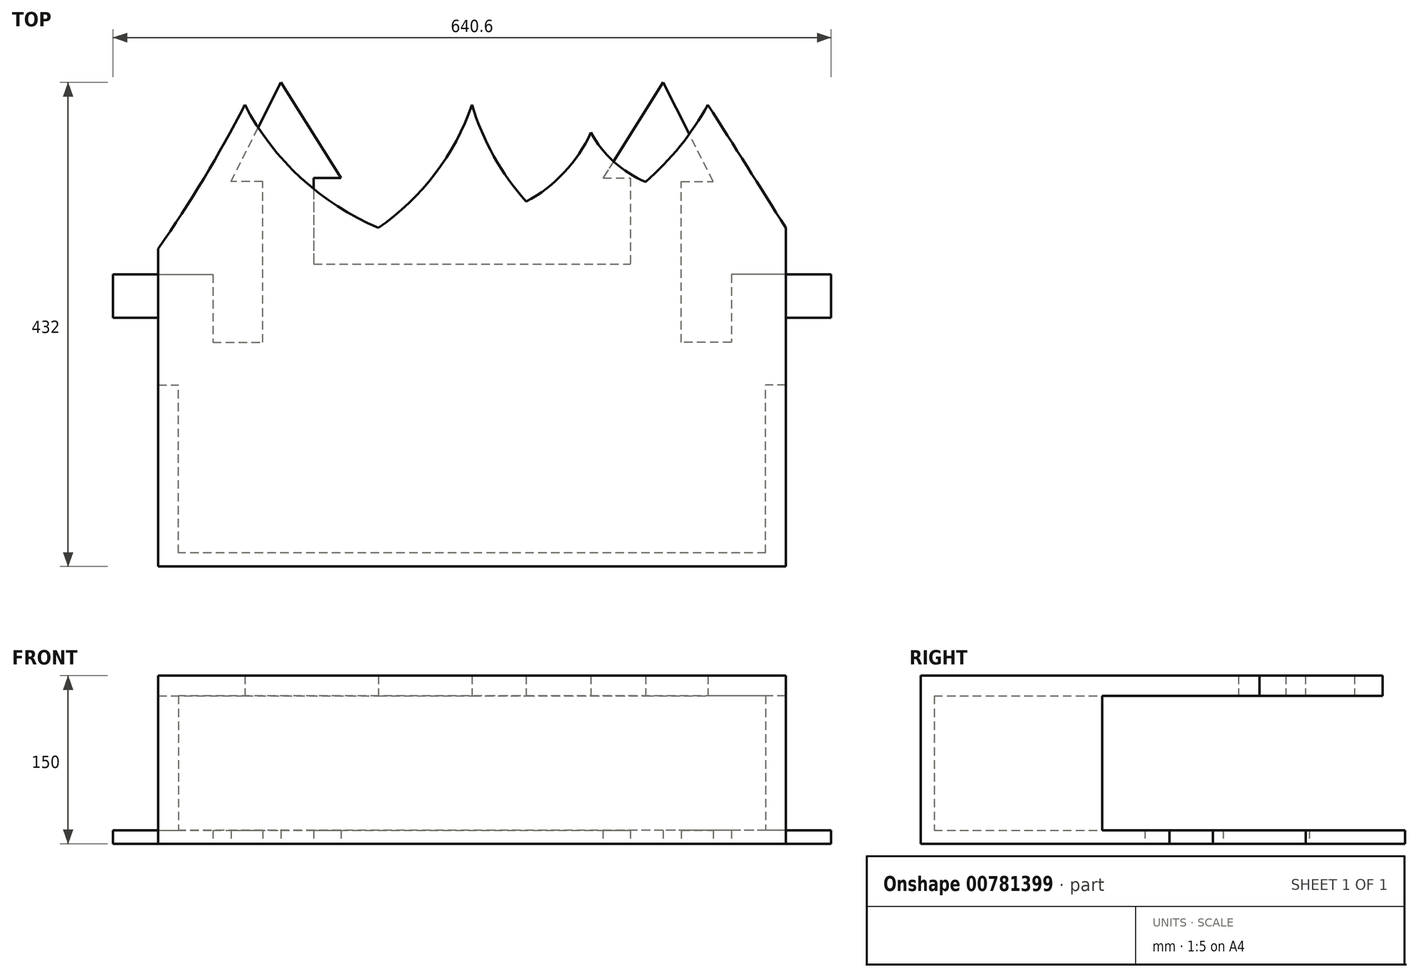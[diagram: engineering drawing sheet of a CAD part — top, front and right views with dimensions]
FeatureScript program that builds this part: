
annotation { "Feature Type Name" : "Feature", "Feature Type Description" : "" }
export const myFeature = defineFeature(function(context is Context, id is Id, definition is map)
    precondition{}
    {
        {
            var Q0;
            Q0=qCreatedBy(makeId("Top.planeOp"),FACE);
            var sketch = newSketch(context, id + "F0", { "sketchPlane" : qUnion([Q0])});
            skLineSegment(sketch, "E0.bottom", {"start": v(0, 0) * mm, "end": v(-280, 0) * mm});
            skLineSegment(sketch, "E0.left", {"start": v(0, 0) * mm, "end": v(0, 257.8) * mm});
            skLineSegment(sketch, "E0.right", {"start": v(-280, 0) * mm, "end": v(-280, 210) * mm});
            skLineSegment(sketch, "E1", {"start": v(-280, 210) * mm, "end": v(-320.3, 210) * mm});
            skLineSegment(sketch, "E2", {"start": v(-320.3, 210) * mm, "end": v(-320.3, 248.7) * mm});
            skLineSegment(sketch, "E3", {"start": v(-320.3, 248.7) * mm, "end": v(-231.27, 248.7) * mm});
            skLineSegment(sketch, "E4", {"start": v(-231.27, 248.7) * mm, "end": v(-231.27, 188) * mm});
            skLineSegment(sketch, "E5", {"start": v(-231.27, 188) * mm, "end": v(-186.75, 188) * mm});
            skLineSegment(sketch, "E6", {"start": v(-186.75, 188) * mm, "end": v(-186.75, 331.66) * mm});
            skLineSegment(sketch, "E7", {"start": v(-186.75, 331.66) * mm, "end": v(-215.08, 331.66) * mm});
            skLineSegment(sketch, "E8", {"start": v(-215.08, 331.66) * mm, "end": v(-170.56, 420) * mm});
            skLineSegment(sketch, "E9", {"start": v(-170.56, 420) * mm, "end": v(-116.94, 334.7) * mm});
            skLineSegment(sketch, "E10", {"start": v(-116.94, 334.7) * mm, "end": v(-141.22, 334.7) * mm});
            skLineSegment(sketch, "E11", {"start": v(-141.22, 334.7) * mm, "end": v(-141.22, 257.8) * mm});
            skLineSegment(sketch, "E12", {"start": v(-141.22, 257.8) * mm, "end": v(0, 257.8) * mm});
            skPoint(sketch, "E13.orphan", {"position": v(-280, 420) * mm});
            skLineSegment(sketch, "E14.MirrorCS", {"start": v(141.22, 257.8) * mm, "end": v(0, 257.8) * mm});
            skLineSegment(sketch, "E15.MirrorCS", {"start": v(141.22, 334.7) * mm, "end": v(141.22, 257.8) * mm});
            skLineSegment(sketch, "E16.MirrorCS", {"start": v(116.94, 334.7) * mm, "end": v(141.22, 334.7) * mm});
            skLineSegment(sketch, "E17.MirrorCS", {"start": v(170.56, 420) * mm, "end": v(116.94, 334.7) * mm});
            skLineSegment(sketch, "E18.MirrorCS", {"start": v(215.08, 331.66) * mm, "end": v(170.56, 420) * mm});
            skLineSegment(sketch, "E19.MirrorCS", {"start": v(186.75, 331.66) * mm, "end": v(215.08, 331.66) * mm});
            skLineSegment(sketch, "E20.MirrorCS", {"start": v(186.75, 188) * mm, "end": v(186.75, 331.66) * mm});
            skLineSegment(sketch, "E21.MirrorCS", {"start": v(231.27, 188) * mm, "end": v(186.75, 188) * mm});
            skLineSegment(sketch, "E22.MirrorCS", {"start": v(231.27, 248.7) * mm, "end": v(231.27, 188) * mm});
            skLineSegment(sketch, "E23.MirrorCS", {"start": v(320.3, 248.7) * mm, "end": v(231.27, 248.7) * mm});
            skLineSegment(sketch, "E24.MirrorCS", {"start": v(320.3, 210) * mm, "end": v(320.3, 248.7) * mm});
            skLineSegment(sketch, "E25.MirrorCS", {"start": v(280, 210) * mm, "end": v(320.3, 210) * mm});
            skLineSegment(sketch, "E26.MirrorCS", {"start": v(280, 0) * mm, "end": v(280, 210) * mm});
            skLineSegment(sketch, "E27.MirrorCS", {"start": v(0, 0) * mm, "end": v(280, 0) * mm});
            skSolve(sketch);
        }
        {
            var Q0;
            Q0 = qSketchRegion(id + "F0", true);
            extrude(context, id + "F1", {"entities" : qUnion([Q0]), "depth" : 12 * mm, "offsetDistance" : 25 * mm});
        }
        {
            var Q0;
            Q0=makeQuery(id+"F1.opExtrude","CAP_FACE",FACE,{"disambiguationData":[OSD([sQuery(id+"F0.wireOp",EDGE,"E0.bottom"),sQuery(id+"F0.wireOp",EDGE,"E0.right"),sQuery(id+"F0.wireOp",EDGE,"E1"),sQuery(id+"F0.wireOp",EDGE,"E2"),sQuery(id+"F0.wireOp",EDGE,"E3"),sQuery(id+"F0.wireOp",EDGE,"E4"),sQuery(id+"F0.wireOp",EDGE,"E5"),sQuery(id+"F0.wireOp",EDGE,"E6"),sQuery(id+"F0.wireOp",EDGE,"E7"),sQuery(id+"F0.wireOp",EDGE,"E8"),sQuery(id+"F0.wireOp",EDGE,"E9"),sQuery(id+"F0.wireOp",EDGE,"E10"),sQuery(id+"F0.wireOp",EDGE,"E11"),sQuery(id+"F0.wireOp",EDGE,"E12"),sQuery(id+"F0.wireOp",EDGE,"E14.MirrorCS"),sQuery(id+"F0.wireOp",EDGE,"E15.MirrorCS"),sQuery(id+"F0.wireOp",EDGE,"E16.MirrorCS"),sQuery(id+"F0.wireOp",EDGE,"E17.MirrorCS"),sQuery(id+"F0.wireOp",EDGE,"E18.MirrorCS"),sQuery(id+"F0.wireOp",EDGE,"E19.MirrorCS"),sQuery(id+"F0.wireOp",EDGE,"E20.MirrorCS"),sQuery(id+"F0.wireOp",EDGE,"E21.MirrorCS"),sQuery(id+"F0.wireOp",EDGE,"E22.MirrorCS"),sQuery(id+"F0.wireOp",EDGE,"E23.MirrorCS"),sQuery(id+"F0.wireOp",EDGE,"E24.MirrorCS"),sQuery(id+"F0.wireOp",EDGE,"E25.MirrorCS"),sQuery(id+"F0.wireOp",EDGE,"E26.MirrorCS"),sQuery(id+"F0.wireOp",EDGE,"E27.MirrorCS")])],"isStart":false});
            var sketch = newSketch(context, id + "F2", { "sketchPlane" : qUnion([Q0])});
            skLineSegment(sketch, "E28.bottom", {"start": v(-280, 0) * mm, "end": v(-262, 0) * mm});
            skLineSegment(sketch, "E28.top", {"start": v(-280, 150) * mm, "end": v(-262, 150) * mm});
            skLineSegment(sketch, "E28.left", {"start": v(-280, 0) * mm, "end": v(-280, 150) * mm});
            skLineSegment(sketch, "E28.right", {"start": v(-262, 0) * mm, "end": v(-262, 150) * mm});
            skLineSegment(sketch, "E29", {"start": v(0, 224.77) * mm, "end": v(0, 107.53) * mm});
            skPoint(sketch, "E29.startSnap0", {"position": v(0, 257.8) * mm});
            skLineSegment(sketch, "E30.MirrorCS", {"start": v(280, 150) * mm, "end": v(262, 150) * mm});
            skLineSegment(sketch, "E31.MirrorCS", {"start": v(262, 0) * mm, "end": v(262, 150) * mm});
            skLineSegment(sketch, "E32.MirrorCS", {"start": v(280, 0) * mm, "end": v(280, 150) * mm});
            skLineSegment(sketch, "E33.MirrorCS", {"start": v(280, 0) * mm, "end": v(262, 0) * mm});
            skSolve(sketch);
        }
        {
            var Q0;
            Q0=makeQuery(id+"F2.imprint","IMPRINT",FACE,{"disambiguationData":[TD([[makeQuery(id+"F2.imprint","IMPRINT",EDGE,{"derivedFrom":sQuery(id+"F2.wireOp",EDGE,"E30.MirrorCS")}),1.0]])]});
            var Q1;
            Q1=makeQuery(id+"F2.imprint","IMPRINT",FACE,{"disambiguationData":[TD([[makeQuery(id+"F2.imprint","IMPRINT",EDGE,{"derivedFrom":sQuery(id+"F2.wireOp",EDGE,"E28.bottom")}),-1.0]])]});
            extrude(context, id + "F3", {"entities" : qUnion([Q0, Q1]), "operationType" : NewBodyOperationType.ADD, "depth" : 120 * mm, "offsetDistance" : 25 * mm});
        }
        {
            var Q0;
            Q0=makeQuery(id+"F3.opExtrude","CAP_FACE",FACE,{"disambiguationData":[OSD([sQuery(id+"F2.wireOp",EDGE,"E28.bottom"),sQuery(id+"F2.wireOp",EDGE,"E28.top"),sQuery(id+"F2.wireOp",EDGE,"E28.left"),sQuery(id+"F2.wireOp",EDGE,"E28.right")])],"isStart":false});
            var sketch = newSketch(context, id + "F4", { "sketchPlane" : qUnion([Q0])});
            skLineSegment(sketch, "E34.bottom", {"start": v(-280, 0) * mm, "end": v(280, 0) * mm});
            skLineSegment(sketch, "E34.top", {"start": v(-280, 400) * mm, "end": v(280, 400) * mm});
            skLineSegment(sketch, "E34.left", {"start": v(-280, 0) * mm, "end": v(-280, 400) * mm});
            skLineSegment(sketch, "E34.right", {"start": v(280, 0) * mm, "end": v(280, 400) * mm});
            skArc(sketch, "E35", {"start": v(-280, 271.66) * mm, "mid": v(-239.23, 334.55) * mm, "end": v(-202.72, 400) * mm});
            skArc(sketch, "E36", {"start": v(-202.72, 400) * mm, "mid": v(-152.67, 334.75) * mm, "end": v(-83.53, 290.23) * mm});
            skArc(sketch, "E37", {"start": v(-83.53, 290.23) * mm, "mid": v(-33.01, 338.45) * mm, "end": v(0, 400) * mm});
            skArc(sketch, "E38", {"start": v(0, 400) * mm, "mid": v(19.47, 354.2) * mm, "end": v(48.36, 313.67) * mm});
            skArc(sketch, "E39", {"start": v(48.36, 313.67) * mm, "mid": v(82.28, 339.67) * mm, "end": v(106, 375.22) * mm});
            skArc(sketch, "E40", {"start": v(106, 375.22) * mm, "mid": v(126.71, 349.11) * mm, "end": v(154.85, 331.26) * mm});
            skArc(sketch, "E41", {"start": v(154.85, 331.26) * mm, "mid": v(185.64, 363.24) * mm, "end": v(210.54, 400) * mm});
            skArc(sketch, "E42", {"start": v(280, 290.23) * mm, "mid": v(245.3, 345.14) * mm, "end": v(210.54, 400) * mm});
            skSolve(sketch);
        }
        {
            var Q0;
            {var subQ4=makeQuery(id+"F3.opExtrude","CAP_EDGE",EDGE,{"disambiguationData":[OSD([sQuery(id+"F2.wireOp",EDGE,"E28.top")])],"isStart":false});Q0=makeQuery(id+"F4.imprint","IMPRINT",FACE,{"disambiguationData":[TD([[makeQuery(id+"F4.imprint","IMPRINT",EDGE,{"derivedFrom":subQ4}),-1.0]])]});}
            var Q1;
            {var subQ2=sQuery(id+"F4.wireOp",EDGE,"E35");Q1=makeQuery(id+"F4.imprint","IMPRINT",FACE,{"disambiguationData":[TD([[makeQuery(id+"F4.imprint","IMPRINT",EDGE,{"derivedFrom":subQ2}),-1.0]])]});}
            extrude(context, id + "F5", {"entities" : qUnion([Q0, Q1]), "operationType" : NewBodyOperationType.ADD, "depth" : 18 * mm, "offsetDistance" : 25 * mm});
        }
        {
            var Q0;
            Q0=makeQuery(id+"F5.boolean.opBoolean","MERGE",FACE,{"derivedFrom":[makeQuery(id+"F3.boolean.opBoolean","MERGE",FACE,{"derivedFrom":[makeQuery(id+"F1.opExtrude","SWEPT_FACE",FACE,{"disambiguationData":[OSD([sQuery(id+"F0.wireOp",EDGE,"E0.bottom"),sQuery(id+"F0.wireOp",EDGE,"E27.MirrorCS")])]}),makeQuery(id+"F3.opExtrude","SWEPT_FACE",FACE,{"disambiguationData":[OSD([sQuery(id+"F2.wireOp",EDGE,"E28.bottom")])]}),makeQuery(id+"F3.opExtrude","SWEPT_FACE",FACE,{"disambiguationData":[OSD([sQuery(id+"F2.wireOp",EDGE,"E33.MirrorCS")])]})]}),makeQuery(id+"F5.opExtrude","SWEPT_FACE",FACE,{"disambiguationData":[OSD([sQuery(id+"F4.wireOp",EDGE,"E34.bottom")])]})]});
            var sketch = newSketch(context, id + "F6", { "sketchPlane" : qUnion([Q0])});
            skLineSegment(sketch, "E43.bottom", {"start": v(280, 0) * mm, "end": v(-280, 0) * mm});
            skLineSegment(sketch, "E43.top", {"start": v(280, 150) * mm, "end": v(-280, 150) * mm});
            skLineSegment(sketch, "E43.left", {"start": v(280, 0) * mm, "end": v(280, 150) * mm});
            skLineSegment(sketch, "E43.right", {"start": v(-280, 0) * mm, "end": v(-280, 150) * mm});
            skSolve(sketch);
        }
        {
            var Q0;
            Q0 = qSketchRegion(id + "F6", true);
            extrude(context, id + "F7", {"entities" : qUnion([Q0]), "operationType" : NewBodyOperationType.ADD, "depth" : 12 * mm, "offsetDistance" : 25 * mm});
        }
    });
